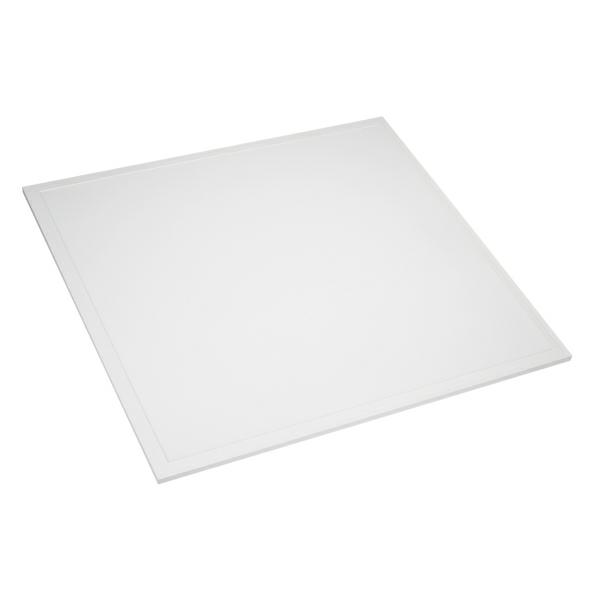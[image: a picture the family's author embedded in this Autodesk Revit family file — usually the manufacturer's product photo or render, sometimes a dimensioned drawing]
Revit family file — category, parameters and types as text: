
# Revit family: TITAN-S600x600
name_source: partatom
category: Осветительные приборы
revit_build: Autodesk Revit 2017 (Build: 20160225_1515(x64)
units: mm (PartAtom-declared; Revit-internal decimal feet)

## family parameters
Всегда вертикально = Да
Источник света = Да
На основе рабочей плоскости = Нет
Общий = Нет
При загрузке вырезать с полостями = Нет
Размер круглого соединителя = Использовать диаметр
Тип детали = Нормальный
Точка расчета площади = Нет

## types (3) — shared parameters
ADSK_Единица измерения = шт.
ADSK_Завод-изготовитель = ARLIGHT
ADSK_Классификация нагрузок = Освещение
ADSK_Количество фаз = 1
ADSK_Количество фаз числовое = 1
ADSK_Коэффициент мощности = 0.95
ADSK_Масса_Текст = 1.75
ADSK_Наименование = Светильник
ADSK_Напряжение = 230 В
ADSK_Номинальная мощность = 40 Вт
ADSK_Полная мощность = 42 В·А
ADSK_Размер_Высота = 31.3 мм
ADSK_Размер_Длина = 595 мм
ADSK_Размер_Ширина = 595 мм
ADSK_Ток = 0 А
ARL_Драйвер = В комплекте (33-40V, 1000mA)
ARL_Индекс цветопередачи = >80
ARL_Класс защиты от поражения электрическим током = II
ARL_Класс пылевлагозащиты = IP20
ARL_Материал корпуса = Металл, белый
ARL_Область использования = Для освещения жилых, офисных, торговых и других помещений
ARL_Обозначение корпуса = Корпус квадратный, металл, цвет белый
ARL_Рабочая температура окружающей среды = -10...+45 °C
ARL_Серия = TITAN
ARL_Способ монтажа = Встраиваемый
ARL_Тип товара = Светильник
ARL_Угол обзора = 120°
ARL_Цвет покрытия = Белый
URL = https://arlight.ru
Видимая форма излучения при визуализации = Нет
Группа модели = Светильники
Изготовитель = ARLIGHT
Изготовитель (сайт) = www.arlight.ru
Изготовитель (телефон) = 8 800 505 26 29
Излучение по длине прямоугольника = 555 мм
Излучение по ширине прямоугольника = 555 мм
Полная установленная мощность = 42 В·А
Разработчик = НТЦ Конструктор
Разработчик (URL) = https://constructor.ru
Разработчик (телефон) = +7 (495) 781-05-35
Светофильтр = 16777215
Смещение цветовой температуры при затухании лампы = <Нет>
Угол наклона = 90.00°

## per-type parameters (varying)
| type | ADSK_Код изделия | ADSK_Марка | ARL_Цвет свечения | Комментарии к типоразмеру | Описание | Файл фотометрической сетки |
| 030302 Светильник DL-TITAN-S600x600-40W Day4000 (WH, 120 deg, 230V) | Арт. 030302 | DL-TITAN-S600x600-40W Day4000 | Дневной 4000K | Арт. 030302 | Светодиодная панель (backlit) белая. Цвет БЕЛЫЙ ДНЕВНОЙ 4000К-4300К, св.поток 4000лм. Питание 100-240VAC, мощность 40 Вт. IP20. Размеры 595x595х31.3 мм. В комплекте: панель, драйвер (33-40V, 1000mA). Подвес приобретается отдельно | 030302_ DL-TITAN-S600x600-40W Day4000 (WH, 120 deg, 230V).ies |
| 030304 Светильник DL-TITAN-S600x600-40W Warm3000 (WH, 120 deg, 230V) | Арт. 030304 | DL-TITAN-S600x600-40W Warm3000 | Теплый 3000K | Арт. 030304 | Светодиодная панель (backlit) белая. Цвет БЕЛЫЙ ТЕПЛЫЙ 3000К, св.поток 4000лм. Питание 100-240VAC, мощность 40 Вт. IP20. Размеры 595x595х31.3 мм. В комплекте: панель, драйвер (33-40V, 1000mA). Подвес приобретается отдельно | 030304_DL-TITAN-S600x600-40W Warm3000 (WH, 120 deg, 230V).ies |
| 030305 Светильник DL-TITAN-S600x600-40W White6000 (WH, 120 deg, 230V) | Арт. 030305 | DL-TITAN-S600x600-40W White6000 | Белый 6000K | Арт. 030305 | Светодиодная панель (backlit) белая. Цвет БЕЛЫЙ 6000К-6800К, св.поток 4000лм. Питание 100-240VAC, мощность 40 Вт. IP20. Размеры 595x595х31.3 мм. В комплекте: панель, драйвер (33-40V, 1000mA). Подвес приобретается отдельно | 030305_ DL-TITAN-S600x600-40W White6000 (WH, 120 deg, 230V).ies |
